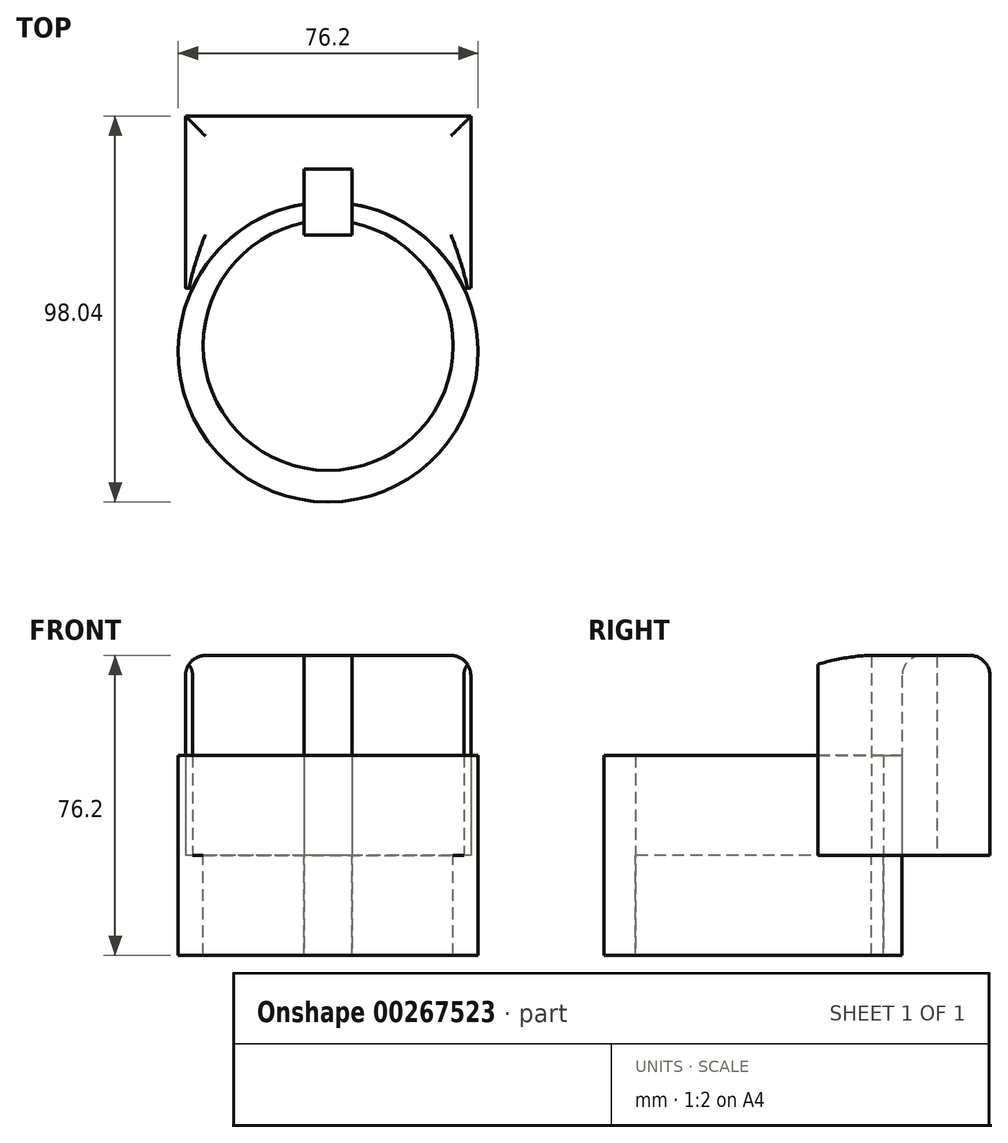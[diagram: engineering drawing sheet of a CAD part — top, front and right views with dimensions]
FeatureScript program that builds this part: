
annotation { "Feature Type Name" : "Feature", "Feature Type Description" : "" }
export const myFeature = defineFeature(function(context is Context, id is Id, definition is map)
    precondition{}
    {
        {
            var Q0;
            Q0=qCreatedBy(makeId("Top.planeOp"),FACE);
            var sketch = newSketch(context, id + "F0", { "sketchPlane" : qUnion([Q0])});
            skCircle(sketch, "E0", {"center": v(0, -1.67) * mm, "radius": 38.1 * mm});
            skLineSegment(sketch, "E1.bottom", {"start": v(36.23, 58.27) * mm, "end": v(-36.23, 58.27) * mm});
            skLineSegment(sketch, "E1.top", {"start": v(36.23, 14.6) * mm, "end": v(-36.23, 14.6) * mm});
            skLineSegment(sketch, "E1.left", {"start": v(36.23, 58.27) * mm, "end": v(36.23, 14.6) * mm});
            skLineSegment(sketch, "E1.right", {"start": v(-36.23, 58.27) * mm, "end": v(-36.23, 14.6) * mm});
            skPoint(sketch, "E1.middle", {"position": v(0, 36.43) * mm});
            skCircle(sketch, "E2", {"center": v(0, 0) * mm, "radius": 31.75 * mm});
            skLineSegment(sketch, "E3.bottom", {"start": v(6.07, 28.1) * mm, "end": v(-6.07, 28.1) * mm});
            skLineSegment(sketch, "E3.top", {"start": v(6.07, 44.76) * mm, "end": v(-6.07, 44.76) * mm});
            skLineSegment(sketch, "E3.left", {"start": v(6.07, 28.1) * mm, "end": v(6.07, 44.76) * mm});
            skLineSegment(sketch, "E3.right", {"start": v(-6.07, 28.1) * mm, "end": v(-6.07, 44.76) * mm});
            skSolve(sketch);
        }
        {
            var Q0;
            Q0=makeQuery(id+"F0.imprint","IMPRINT",FACE,{"disambiguationData":[TD([[makeQuery(id+"F0.imprint","IMPRINT",EDGE,{"derivedFrom":sQuery(id+"F0.wireOp",EDGE,"E1.bottom")}),1.0]])]});
            extrude(context, id + "F1", {"entities" : qUnion([Q0]), "depth" : 50.8 * mm});
        }
        {
            var Q0;
            {var subQ0=sQuery(id+"F0.wireOp",EDGE,"E1.top");var subQ1=sQuery(id+"F0.wireOp",EDGE,"E0");var subQ2=makeQuery(id+"F0.imprint","INTERSECT",VERTEX,{"disambiguationData":[OD(0.0)],"derivedFrom":[subQ1,subQ0]});Q0=makeQuery(id+"F0.imprint","IMPRINT",FACE,{"disambiguationData":[TD([[makeQuery(id+"F0.imprint","IMPRINT",EDGE,{"disambiguationData":[TD([[subQ2,1.0]])],"derivedFrom":subQ1}),1.0]])]});}
            var Q1;
            {var subQ0=sQuery(id+"F0.wireOp",EDGE,"E1.top");var subQ1=sQuery(id+"F0.wireOp",EDGE,"E0");var subQ2=makeQuery(id+"F0.imprint","INTERSECT",VERTEX,{"disambiguationData":[OD(0.0)],"derivedFrom":[subQ1,subQ0]});Q1=makeQuery(id+"F0.imprint","IMPRINT",FACE,{"disambiguationData":[TD([[makeQuery(id+"F0.imprint","IMPRINT",EDGE,{"disambiguationData":[TD([[subQ2,-1.0]])],"derivedFrom":subQ1}),1.0]])]});}
            var Q2;
            {var subQ0=sQuery(id+"F0.wireOp",EDGE,"E1.top");var subQ1=sQuery(id+"F0.wireOp",EDGE,"E0");var subQ2=makeQuery(id+"F0.imprint","INTERSECT",VERTEX,{"disambiguationData":[OD(1.0)],"derivedFrom":[subQ1,subQ0]});Q2=makeQuery(id+"F0.imprint","IMPRINT",FACE,{"disambiguationData":[TD([[makeQuery(id+"F0.imprint","IMPRINT",EDGE,{"disambiguationData":[TD([[subQ2,1.0]])],"derivedFrom":subQ1}),1.0]])]});}
            extrude(context, id + "F2", {"entities" : qUnion([Q0, Q1, Q2]), "endBound" : BoundingType.SYMMETRIC, "depth" : 50.8 * mm});
        }
        {
            var Q0;
            {var subQ0=sQuery(id+"F0.wireOp",EDGE,"E2");var subQ1=sQuery(id+"F0.wireOp",EDGE,"E1.top");var subQ2=makeQuery(id+"F0.imprint","INTERSECT",VERTEX,{"disambiguationData":[OD(0.0)],"derivedFrom":[subQ1,subQ0]});Q0=makeQuery(id+"F0.imprint","IMPRINT",FACE,{"disambiguationData":[TD([[makeQuery(id+"F0.imprint","IMPRINT",EDGE,{"disambiguationData":[TD([[subQ2,-1.0]])],"derivedFrom":subQ1}),1.0]])]});}
            var Q1;
            {var subQ0=sQuery(id+"F0.wireOp",EDGE,"E2");var subQ1=sQuery(id+"F0.wireOp",EDGE,"E1.top");var subQ2=makeQuery(id+"F0.imprint","INTERSECT",VERTEX,{"disambiguationData":[OD(0.0)],"derivedFrom":[subQ1,subQ0]});Q1=makeQuery(id+"F0.imprint","IMPRINT",FACE,{"disambiguationData":[TD([[makeQuery(id+"F0.imprint","IMPRINT",EDGE,{"disambiguationData":[TD([[subQ2,-1.0]])],"derivedFrom":subQ1}),-1.0]])]});}
            extrude(context, id + "F3", {"entities" : qUnion([Q0, Q1]), "oppositeDirection" : true, "depth" : 25.4 * mm});
        }
        {
            var Q0;
            Q0=makeQuery(id+"F1.opExtrude","CAP_EDGE",EDGE,{"disambiguationData":[OSD([sQuery(id+"F0.wireOp",EDGE,"E1.bottom")])],"isStart":false});
            var Q1;
            Q1=makeQuery(id+"F1.opExtrude","CAP_EDGE",EDGE,{"disambiguationData":[OSD([sQuery(id+"F0.wireOp",EDGE,"E1.left")])],"isStart":false});
            var Q2;
            Q2=makeQuery(id+"F1.opExtrude","CAP_EDGE",EDGE,{"disambiguationData":[OSD([sQuery(id+"F0.wireOp",EDGE,"E1.right")])],"isStart":false});
            var Q3;
            Q3=makeQuery(id+"F1.opExtrude","CAP_EDGE",EDGE,{"disambiguationData":[OSD([sQuery(id+"F0.wireOp",EDGE,"E0")])],"isStart":false});
            fillet(context, id + "F4", {"entities" : qUnion([Q0, Q1, Q2, Q3]), "radius" : 5.08 * mm, "tangentPropagation" : true, "allowEdgeOverflow" : false});
        }
        {
            var Q0;
            {var subQ0=sQuery(id+"F0.wireOp",EDGE,"E3.left");var subQ1=sQuery(id+"F0.wireOp",EDGE,"E0");var subQ2=makeQuery(id+"F0.imprint","INTERSECT",VERTEX,{"derivedFrom":[subQ1,subQ0]});Q0=makeQuery(id+"F0.imprint","IMPRINT",FACE,{"disambiguationData":[TD([[makeQuery(id+"F0.imprint","IMPRINT",EDGE,{"disambiguationData":[TD([[subQ2,-1.0]])],"derivedFrom":subQ1}),1.0]])]});}
            var Q1;
            {var subQ5=sQuery(id+"F0.wireOp",EDGE,"E3.top");Q1=makeQuery(id+"F0.imprint","IMPRINT",FACE,{"disambiguationData":[TD([[makeQuery(id+"F0.imprint","IMPRINT",EDGE,{"derivedFrom":subQ5}),1.0]])]});}
            var Q2;
            {var subQ5=sQuery(id+"F0.wireOp",EDGE,"E3.bottom");Q2=makeQuery(id+"F0.imprint","IMPRINT",FACE,{"disambiguationData":[TD([[makeQuery(id+"F0.imprint","IMPRINT",EDGE,{"derivedFrom":subQ5}),-1.0]])]});}
            extrude(context, id + "F5", {"entities" : qUnion([Q0, Q1, Q2]), "depth" : 50.8 * mm});
        }
    });
